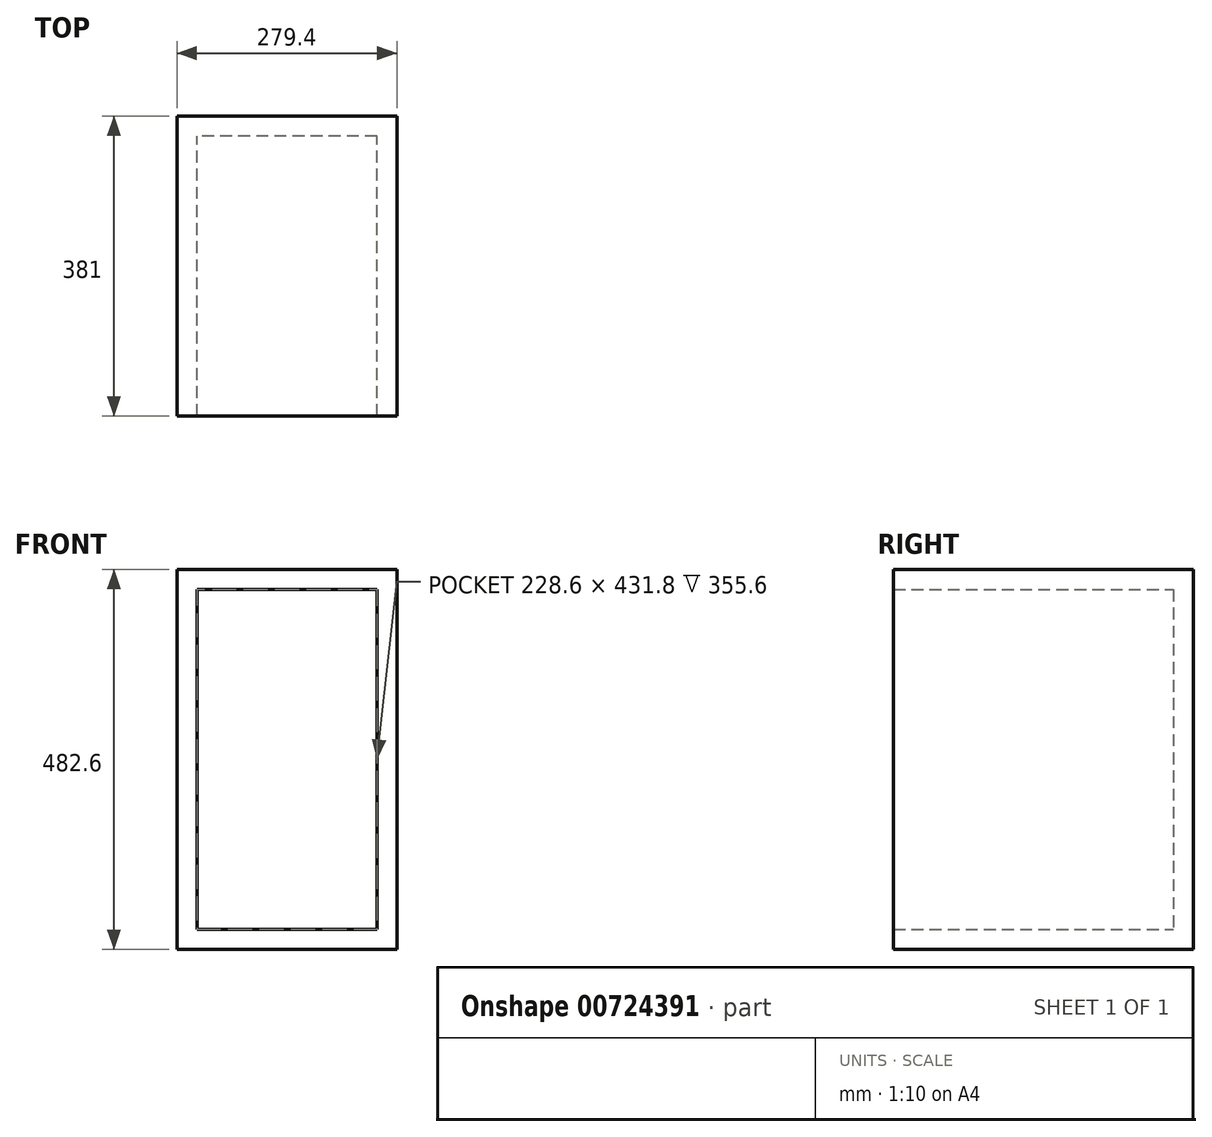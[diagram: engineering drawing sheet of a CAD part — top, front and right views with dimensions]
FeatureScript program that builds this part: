
annotation { "Feature Type Name" : "Feature", "Feature Type Description" : "" }
export const myFeature = defineFeature(function(context is Context, id is Id, definition is map)
    precondition{}
    {
        {
            var Q0;
            Q0=qCreatedBy(makeId("Front.planeOp"),FACE);
            var sketch = newSketch(context, id + "F0", { "sketchPlane" : qUnion([Q0])});
            skLineSegment(sketch, "E0.bottom", {"start": v(139.7, 241.3) * mm, "end": v(-139.7, 241.3) * mm});
            skLineSegment(sketch, "E0.top", {"start": v(139.7, -241.3) * mm, "end": v(-139.7, -241.3) * mm});
            skLineSegment(sketch, "E0.left", {"start": v(139.7, 241.3) * mm, "end": v(139.7, -241.3) * mm});
            skLineSegment(sketch, "E0.right", {"start": v(-139.7, 241.3) * mm, "end": v(-139.7, -241.3) * mm});
            skPoint(sketch, "E0.middle", {"position": v(0, 0) * mm});
            skSolve(sketch);
        }
        {
            var Q0;
            Q0 = qSketchRegion(id + "F0", true);
            extrude(context, id + "F1", {"entities" : qUnion([Q0]), "depth" : 381 * mm, "offsetDistance" : 25.4 * mm});
        }
        {
            var Q0;
            Q0=makeQuery(id+"F1.opExtrude","CAP_FACE",FACE,{"disambiguationData":[OSD([sQuery(id+"F0.wireOp",EDGE,"E0.bottom"),sQuery(id+"F0.wireOp",EDGE,"E0.top"),sQuery(id+"F0.wireOp",EDGE,"E0.left"),sQuery(id+"F0.wireOp",EDGE,"E0.right")])],"isStart":false});
            var Q1;
            Q1=makeQuery(id+"F1.opExtrude","SWEPT_BODY",BODY,{"disambiguationData":[OSD([sQuery(id+"F0.wireOp",EDGE,"E0.bottom"),sQuery(id+"F0.wireOp",EDGE,"E0.top"),sQuery(id+"F0.wireOp",EDGE,"E0.left"),sQuery(id+"F0.wireOp",EDGE,"E0.right")])]});
            shell(context, id + "F2", {"entities" : qUnion([Q0]), "parts" : qUnion([Q1]), "thickness" : 25.4 * mm});
        }
    });
